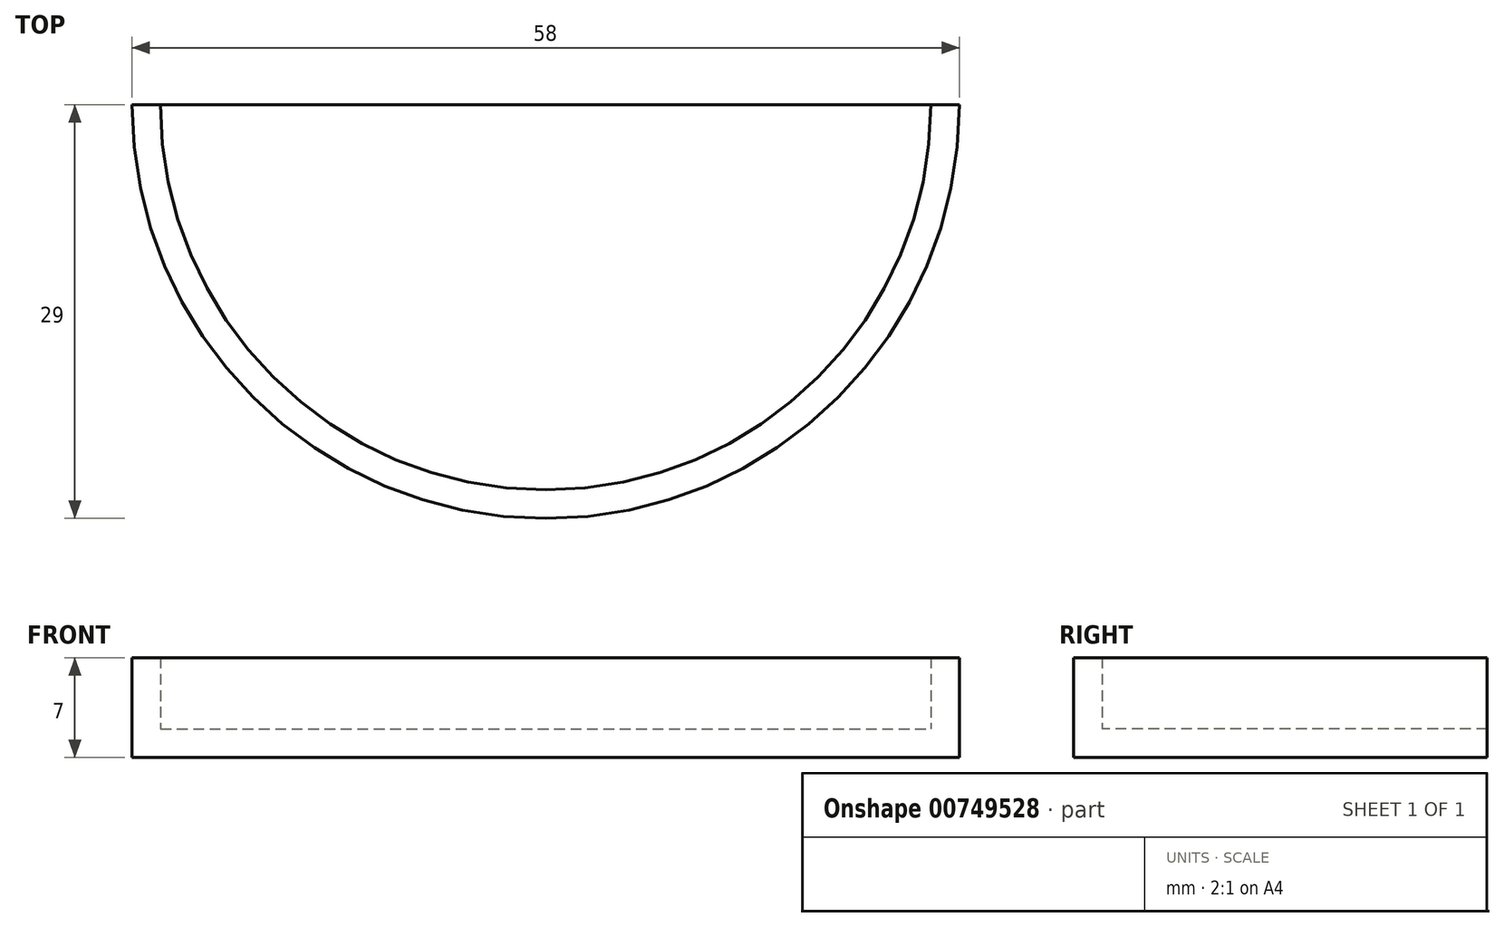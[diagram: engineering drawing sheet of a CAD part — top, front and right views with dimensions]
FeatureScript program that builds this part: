
annotation { "Feature Type Name" : "Feature", "Feature Type Description" : "" }
export const myFeature = defineFeature(function(context is Context, id is Id, definition is map)
    precondition{}
    {
        {
            var Q0;
            Q0=qCreatedBy(makeId("Top.planeOp"),FACE);
            var sketch = newSketch(context, id + "F0", { "sketchPlane" : qUnion([Q0])});
            skArc(sketch, "E0", {"start": v(-29, -45) * mm, "mid": v(0, -74) * mm, "end": v(29, -45) * mm});
            skLineSegment(sketch, "E1", {"start": v(-29, -45) * mm, "end": v(-27, -45) * mm});
            skLineSegment(sketch, "E2", {"start": v(27, -45) * mm, "end": v(29, -45) * mm});
            skLineSegment(sketch, "E3", {"start": v(-27, -45) * mm, "end": v(27, -45) * mm});
            skSolve(sketch);
        }
        {
            var Q0;
            Q0=makeQuery(id+"F0.imprint","IMPRINT",FACE,{"disambiguationData":[TD([[makeQuery(id+"F0.imprint","IMPRINT",EDGE,{"derivedFrom":sQuery(id+"F0.wireOp",EDGE,"E0")}),1.0]])]});
            extrude(context, id + "F1", {"entities" : qUnion([Q0]), "depth" : 2 * mm, "offsetDistance" : 25 * mm});
        }
        {
            var Q0;
            {var subQ0=sQuery(id+"F0.wireOp",EDGE,"0Ro1BS0Q-2mgt-ZydI-AfPz-EH0e96b9fWh7");var subQ1=sQuery(id+"F0.wireOp",EDGE,"rKy58ZlB-kP61-Ok1W-jxmB-2eYKyQ9vMdYR");var subQ2=sQuery(id+"F0.wireOp",EDGE,"wOU9iw42-VmFE-qvLC-MN51-g1PPFttMSv0t");var subQ3=sQuery(id+"F0.wireOp",EDGE,"E0");var subQ4=sQuery(id+"F0.wireOp",EDGE,"558eb726-6cf2-43e1-bdee-a8c6296b0cb8");var subQ5=sQuery(id+"F0.wireOp",EDGE,"ba73d0de-0e2d-409b-9d93-c4157ddcb41b");Q0=makeQuery(id+"FiiagdcVel1GEL0_3.boolean.opBoolean","SPLIT",FACE,{"disambiguationData":[TD([makeQuery(id+"F1.opExtrude","SWEPT_FACE",FACE,{"disambiguationData":[OSD([subQ3])]})])],"derivedFrom":makeQuery(id+"F1.opExtrude","CAP_FACE",FACE,{"disambiguationData":[OSD([subQ3,subQ1,subQ0,subQ2,sQuery(id+"F0.wireOp",EDGE,"XkKQgeCp-ePNv-hplC-1Qyw-HeD6xplKxbZk"),subQ4,subQ5])],"isStart":false})});}
            var sketch = newSketch(context, id + "F2", { "sketchPlane" : qUnion([Q0])});
            skArc(sketch, "E4.2", {"start": v(-27, -45) * mm, "mid": v(0, -72) * mm, "end": v(27, -45) * mm});
            skLineSegment(sketch, "E5", {"start": v(27, -45) * mm, "end": v(-29, -45) * mm});
            skLineSegment(sketch, "E6", {"start": v(-29, -45) * mm, "end": v(-27, -45) * mm});
            skSolve(sketch);
        }
        {
            var Q0;
            Q0=makeQuery(id+"F2.imprint","IMPRINT",FACE,{"disambiguationData":[TD([[makeQuery(id+"F2.imprint","IMPRINT",EDGE,{"derivedFrom":sQuery(id+"F2.wireOp",EDGE,"E4.2")}),-1.0]])]});
            extrude(context, id + "F3", {"entities" : qUnion([Q0]), "operationType" : NewBodyOperationType.ADD, "depth" : 5 * mm, "offsetDistance" : 25 * mm});
        }
    });
